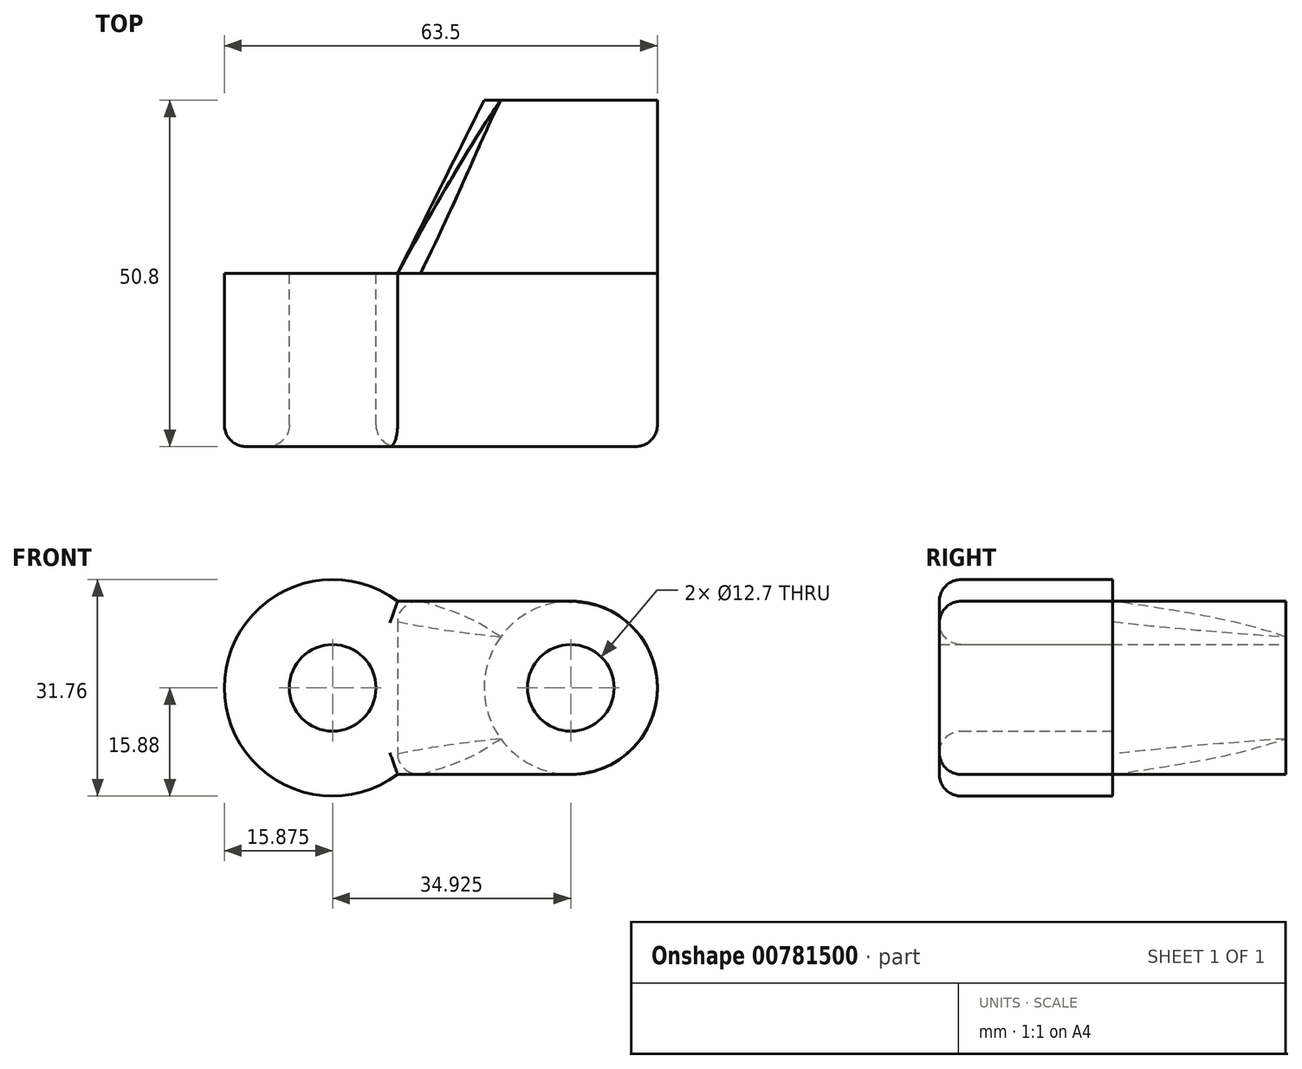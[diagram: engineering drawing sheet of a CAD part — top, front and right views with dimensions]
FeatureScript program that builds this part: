
annotation { "Feature Type Name" : "Feature", "Feature Type Description" : "" }
export const myFeature = defineFeature(function(context is Context, id is Id, definition is map)
    precondition{}
    {
        {
            var Q0;
            Q0=qCreatedBy(makeId("Front.planeOp"),FACE);
            var sketch = newSketch(context, id + "F0", { "sketchPlane" : qUnion([Q0])});
            skCircle(sketch, "E0", {"center": v(0, 0) * mm, "radius": 12.7 * mm});
            skPoint(sketch, "E1", {"position": v(12.7, 0) * mm});
            skPoint(sketch, "E2", {"position": v(0, 12.7) * mm});
            skPoint(sketch, "E3", {"position": v(-12.7, 0) * mm});
            skPoint(sketch, "E4", {"position": v(0, -12.7) * mm});
            skSolve(sketch);
        }
        {
            var Q0;
            Q0=qCreatedBy(makeId("Front.planeOp"),FACE);
            cPlane(context, id + "F1", {"entities" : qUnion([Q0]), "cplaneType" : CPlaneType.OFFSET, "offset" : 25.4 * mm, "width" : 152.4 * mm, "height" : 152.4 * mm});
        }
        {
            var Q0;
            Q0=qCreatedBy(id+"F1.planeOp",FACE);
            var sketch = newSketch(context, id + "F2", { "sketchPlane" : qUnion([Q0])});
            skLineSegment(sketch, "E5", {"start": v(0, 12.7) * mm, "end": v(-25.4, 12.7) * mm});
            skArc(sketch, "E6", {"start": v(0, -12.7) * mm, "mid": v(12.7, 0) * mm, "end": v(0, 12.7) * mm});
            skLineSegment(sketch, "E7", {"start": v(-25.4, -12.7) * mm, "end": v(0, -12.7) * mm});
            skLineSegment(sketch, "E8", {"start": v(-25.4, 12.7) * mm, "end": v(-25.4, -12.7) * mm});
            skPoint(sketch, "E9", {"position": v(12.7, 0) * mm});
            skSolve(sketch);
        }
        {
            var Q0;
            Q0=makeQuery(id+"F0.imprint","IMPRINT",FACE,{"disambiguationData":[TD([[makeQuery(id+"F0.imprint","IMPRINT",EDGE,{"derivedFrom":sQuery(id+"F0.wireOp",EDGE,"E0")}),1.0]])]});
            var Q1;
            Q1=makeQuery(id+"F2.imprint","IMPRINT",FACE,{"disambiguationData":[TD([[makeQuery(id+"F2.imprint","IMPRINT",EDGE,{"derivedFrom":sQuery(id+"F2.wireOp",EDGE,"E5")}),1.0]])]});
            var Q2;
            Q2=sQuery(id+"F0.wireOp",VERTEX,"E1");
            var Q3;
            Q3=sQuery(id+"F2.wireOp",VERTEX,"E9");
            loft(context, id + "F3", {"sheetProfilesArray" : [{ "sheetProfileEntities" : qUnion([Q0]) }, { "sheetProfileEntities" : qUnion([Q1]) }], "matchConnections" : true, "connections" : [{ "connectionEntities" : qUnion([Q2, Q3]), "connectionEdgeQueries" : qUnion([]), "connectionEdgeParameters" : [] }]});
        }
        {
            var Q0;
            Q0=makeQuery(id+"F3.opLoft","CAP_FACE",FACE,{"disambiguationData":[OSD([makeQuery(id+"F2.imprint","IMPRINT",FACE,{"disambiguationData":[TD([[makeQuery(id+"F2.imprint","IMPRINT",EDGE,{"derivedFrom":sQuery(id+"F2.wireOp",EDGE,"E5")}),1.0]])]})])],"isStart":true});
            var sketch = newSketch(context, id + "F4", { "sketchPlane" : qUnion([Q0])});
            skLineSegment(sketch, "E10.bottom", {"start": v(0, 12.7) * mm, "end": v(-25.4, 12.7) * mm});
            skLineSegment(sketch, "E10.top", {"start": v(0, -12.7) * mm, "end": v(-25.4, -12.7) * mm});
            skPoint(sketch, "E10.middle", {"position": v(-12.7, 0) * mm});
            skArc(sketch, "E11", {"start": v(0, -12.7) * mm, "mid": v(12.7, 0) * mm, "end": v(0, 12.7) * mm});
            skArc(sketch, "E12", {"start": v(-25.4, 12.7) * mm, "mid": v(-50.8, 0) * mm, "end": v(-25.4, -12.7) * mm});
            skCircle(sketch, "E13", {"center": v(-34.92, 0) * mm, "radius": 6.35 * mm});
            skSolve(sketch);
        }
        {
            var Q0;
            Q0=makeQuery(id+"F4.imprint","IMPRINT",FACE,{"disambiguationData":[TD([[makeQuery(id+"F4.imprint","IMPRINT",EDGE,{"derivedFrom":sQuery(id+"F4.wireOp",EDGE,"E12")}),1.0]])]});
            var Q1;
            {var subQ2=sQuery(id+"F4.wireOp",EDGE,"E10.bottom");Q1=makeQuery(id+"F4.imprint","IMPRINT",FACE,{"disambiguationData":[TD([[makeQuery(id+"F4.imprint","IMPRINT",EDGE,{"derivedFrom":subQ2}),1.0]])]});}
            extrude(context, id + "F5", {"entities" : qUnion([Q0, Q1]), "operationType" : NewBodyOperationType.ADD, "depth" : 25.4 * mm, "offsetDistance" : 25.4 * mm});
        }
        {
            var Q0;
            Q0=makeQuery(id+"F5.opExtrude","CAP_FACE",FACE,{"disambiguationData":[OSD([sQuery(id+"F4.wireOp",EDGE,"E10.bottom"),sQuery(id+"F4.wireOp",EDGE,"E10.top"),sQuery(id+"F4.wireOp",EDGE,"E11"),sQuery(id+"F4.wireOp",EDGE,"E12"),sQuery(id+"F4.wireOp",EDGE,"E13")])],"isStart":false});
            fillet(context, id + "F6", {"entities" : qUnion([Q0]), "radius" : 3.17 * mm, "tangentPropagation" : true, "allowEdgeOverflow" : false});
        }
        {
            var Q0;
            Q0=makeQuery(id+"F3.opLoft","CAP_FACE",FACE,{"disambiguationData":[OSD([makeQuery(id+"F0.imprint","IMPRINT",FACE,{"disambiguationData":[TD([[makeQuery(id+"F0.imprint","IMPRINT",EDGE,{"derivedFrom":sQuery(id+"F0.wireOp",EDGE,"E0")}),1.0]])]})])],"isStart":true});
            var sketch = newSketch(context, id + "F7", { "sketchPlane" : qUnion([Q0])});
            skCircle(sketch, "E14", {"center": v(0, 0) * mm, "radius": 6.35 * mm});
            skSolve(sketch);
        }
        {
            var Q0;
            Q0=makeQuery(id+"F7.imprint","IMPRINT",FACE,{"disambiguationData":[TD([[makeQuery(id+"F7.imprint","IMPRINT",EDGE,{"derivedFrom":sQuery(id+"F7.wireOp",EDGE,"E14")}),1.0]])]});
            var Q1;
            Q1=makeQuery(id+"F5.opExtrude","CAP_FACE",FACE,{"disambiguationData":[OSD([sQuery(id+"F4.wireOp",EDGE,"E10.bottom"),sQuery(id+"F4.wireOp",EDGE,"E10.top"),sQuery(id+"F4.wireOp",EDGE,"E11"),sQuery(id+"F4.wireOp",EDGE,"E12"),sQuery(id+"F4.wireOp",EDGE,"E13")])],"isStart":false});
            extrude(context, id + "F8", {"entities" : qUnion([Q0]), "operationType" : NewBodyOperationType.REMOVE, "endBound" : BoundingType.UP_TO_SURFACE, "oppositeDirection" : true, "depth" : 25.4 * mm, "endBoundEntityFace" : qUnion([Q1]), "offsetDistance" : 25.4 * mm});
        }
        {
            var Q0;
            Q0=makeQuery(id+"F3.opLoft","SWEPT_EDGE",EDGE,{"disambiguationData":[OSD([sQuery(id+"F0.wireOp",EDGE,"E0"),sQuery(id+"F2.wireOp",EDGE,"E5"),sQuery(id+"F2.wireOp",EDGE,"E6"),sQuery(id+"F2.wireOp",EDGE,"E8")])]});
            var Q1;
            Q1=makeQuery(id+"F3.opLoft","SWEPT_EDGE",EDGE,{"disambiguationData":[OSD([sQuery(id+"F0.wireOp",EDGE,"E0"),sQuery(id+"F2.wireOp",EDGE,"E5"),sQuery(id+"F2.wireOp",EDGE,"E7"),sQuery(id+"F2.wireOp",EDGE,"E8")])]});
            fillet(context, id + "F9", {"entities" : qUnion([Q0, Q1]), "radius" : 3.17 * mm, "tangentPropagation" : true, "allowEdgeOverflow" : false});
        }
    });
